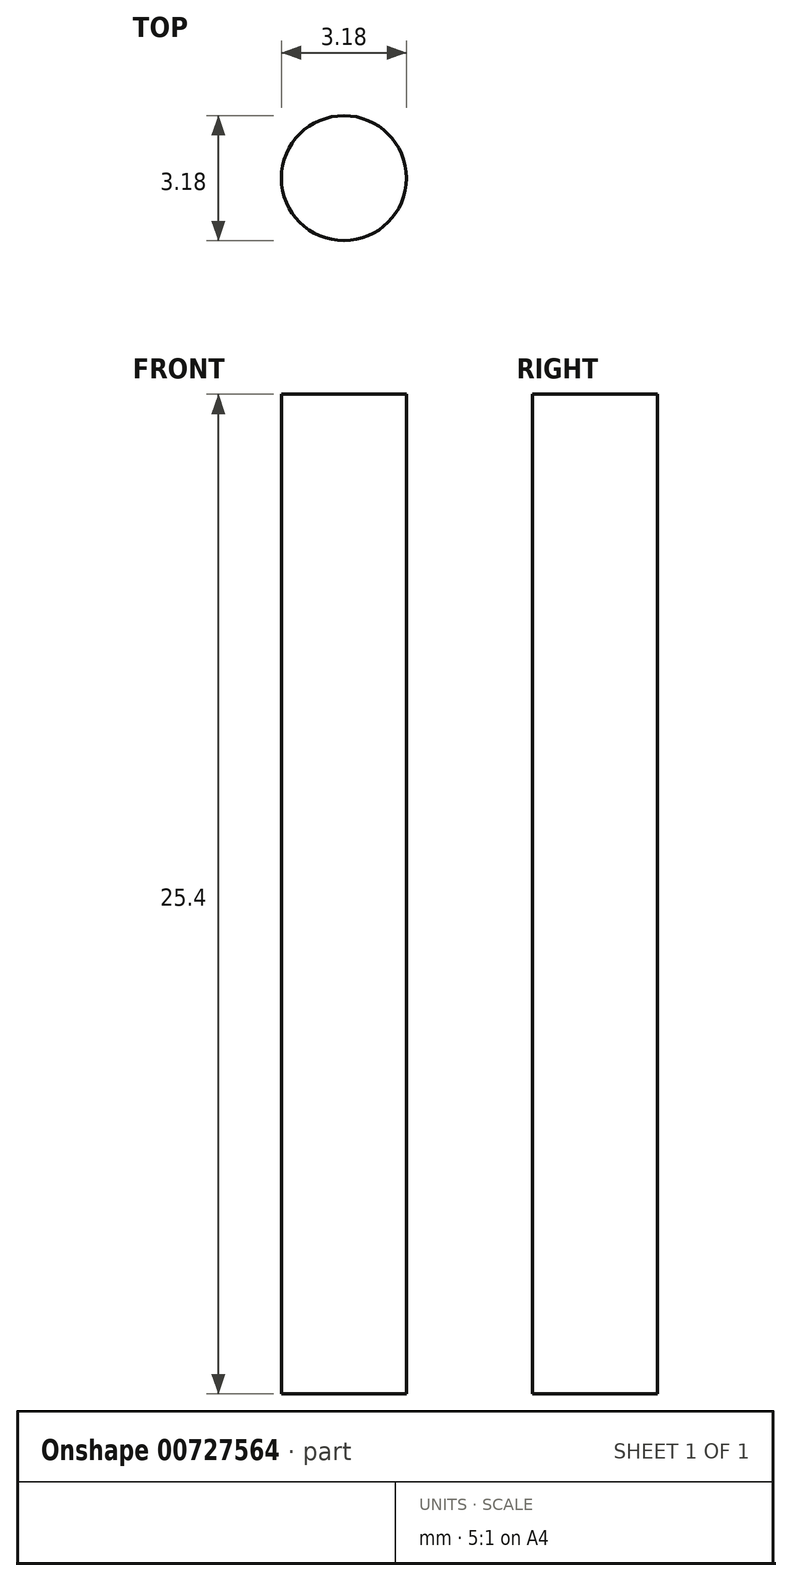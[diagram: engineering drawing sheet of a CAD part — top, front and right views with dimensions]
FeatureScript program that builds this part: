
annotation { "Feature Type Name" : "Feature", "Feature Type Description" : "" }
export const myFeature = defineFeature(function(context is Context, id is Id, definition is map)
    precondition{}
    {
        {
            var Q0;
            Q0=qCreatedBy(makeId("Top.planeOp"),FACE);
            var sketch = newSketch(context, id + "F0", { "sketchPlane" : qUnion([Q0])});
            skCircle(sketch, "E0", {"center": v(0, 0) * mm, "radius": 1.59 * mm});
            skSolve(sketch);
        }
        {
            var Q0;
            Q0=makeQuery(id+"F0.imprint","IMPRINT",FACE,{"disambiguationData":[TD([[makeQuery(id+"F0.imprint","IMPRINT",EDGE,{"derivedFrom":sQuery(id+"F0.wireOp",EDGE,"E0")}),1.0]])]});
            extrude(context, id + "F1", {"entities" : qUnion([Q0]), "depth" : 25.4 * mm, "offsetDistance" : 25.4 * mm});
        }
    });
